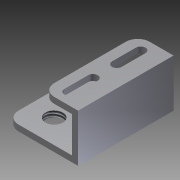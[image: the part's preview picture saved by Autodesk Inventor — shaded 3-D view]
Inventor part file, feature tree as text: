
AUTODESK INVENTOR PART (.ipt)
format: ipt  version: 2012 (Build 160160000, 160)  size: 133,120 bytes
history: native  units: in
note: dims shown in document units (in); Inventor stores cm internally (conversion verified against a paired STEP export)
features: extrude x3, sketch x3, thread x1, fillet x1
ambient origin geometry x8: Origin, YZ Plane, XZ Plane, XY Plane, X Axis, Y Axis, Z Axis, Center Point
bodies: Solid1 (feature_tree)
feature tree (8):
  extrude  "Extrusion1"  Depth=0.125in
  extrude  "Extrusion2"  Depth=2.0in TaperAngle=0.0deg
  thread  "Thread1"  [1 undecoded]
  extrude  "Extrusion3"  Depth=0.5in
  fillet  "Fillet1"  Radius=2.0in
  sketch  "Sketch1"  dims[d2=0.125in d3=0.125in]
  sketch  "Sketch2"  dims[d4=0.125in d7=2.0in d8=0.0in d9=0.366in]
  sketch  "Sketch3"  dims[d10=0.875in d11=0.5in d12=2.0in d13=0.0in d14=1.0in d15=0.0in d16=0.75in d17=1.5in d18=1.375in d19=0.625in d20=1.0in d21=0.5in d22=0.2in d23=1.25in d24=0.4375in d25=0.7874in d27=1.0in d28=0.3937in d30=1.0in d32=0.5in d33=0.0in d34=0.25in]
note: 1 required parameter value undecoded (feature->parameter linkage not recoverable at this tier; creation-order binding heuristic only, values carry confidence <= 0.55)
